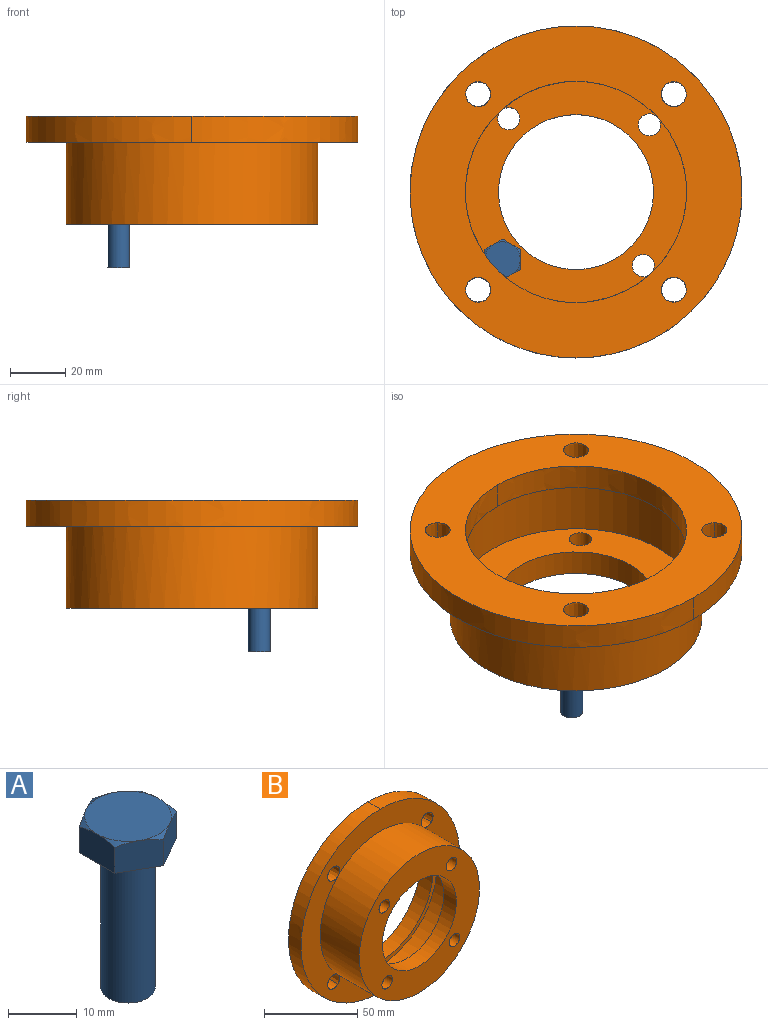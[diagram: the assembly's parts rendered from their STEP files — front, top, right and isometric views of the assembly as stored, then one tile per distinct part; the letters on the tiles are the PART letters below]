
ASSEMBLY  parts=2 mates=1
PART A: 16 faces, bbox 15.3x15.3x31.2 mm
  f0: cylinder r=3.97mm len=25.4mm, axis (0,0,-1), area 633.4mm2, adj f1,f2
  f1: plane 7.94x7.94mm, normal (0,0,-1), area 49.5mm2, adj f0
  f2: plane 14.66x12.7mm, normal (0,0,-1), area 90.2mm2, adj f0,f3,f4,f5,f6,f7,f8
  f3: plane 6.95x5.77mm, normal (-0.5,0.87,0), area 36.4mm2, adj f2,f4,f8,f12,f13
  f4: plane 7.94x5.77mm, normal (-1,0,0), area 36.4mm2, adj f2,f3,f5,f11,f12
  f5: plane 6.95x5.77mm, normal (-0.5,-0.87,0), area 36.4mm2, adj f2,f4,f6,f10,f11
  f6: plane 6.95x5.77mm, normal (0.5,-0.87,0), area 36.4mm2, adj f2,f5,f7,f9,f10
  f7: plane 7.94x5.77mm, normal (1,0,0), area 36.4mm2, adj f2,f6,f8,f9,f14
  f8: plane 6.95x5.77mm, normal (0.5,0.87,0), area 36.4mm2, adj f2,f3,f7,f13,f14
  f9: cone r=6.35mm half-angle=60deg, axis (0,0,-1), area 4mm2, adj f6,f7,f15
  f10: cone r=6.35mm half-angle=60deg, axis (0,0,-1), area 4mm2, adj f5,f6,f15
  f11: cone r=6.35mm half-angle=60deg, axis (0,0,-1), area 4mm2, adj f4,f5,f15
  f12: cone r=6.35mm half-angle=60deg, axis (0,0,-1), area 4mm2, adj f3,f4,f15
  f13: cone r=6.35mm half-angle=60deg, axis (0,0,-1), area 4mm2, adj f3,f8,f15
  f14: cone r=6.35mm half-angle=60deg, axis (0,0,-1), area 4mm2, adj f7,f8,f15
  f15: plane 12.7x12.7mm, normal (0,0,1), area 126.7mm2, adj f9,f10,f11,f12,f13,f14
PART B: 24 faces, bbox 120x39.1x120 mm
  f0: plane 85.01x85.01mm, normal (0,-1,0), area 647.8mm2, adj f10,f12,f15
  f1: extruded ~9.53x7.68mm, area 134.6mm2, adj f6,f11,f14
  f2: extruded ~9.53x7.68mm, area 134.6mm2, adj f7,f11,f14
  f3: extruded ~9.53x7.68mm, area 134.6mm2, adj f8,f11,f14
  f4: extruded ~9.53x7.68mm, area 134.6mm2, adj f9,f11,f14
  f5: extruded ~120x60mm, area 1795.4mm2, adj f11,f13,f14
  f6: extruded ~9.53x7.68mm, area 134.6mm2, adj f1,f11,f14
  f7: extruded ~9.53x7.68mm, area 134.6mm2, adj f2,f11,f14
  f8: extruded ~9.53x7.68mm, area 134.6mm2, adj f3,f11,f14
  f9: extruded ~9.53x7.68mm, area 134.6mm2, adj f4,f11,f14
  f10: extruded ~80x40mm, area 1196.9mm2, adj f0,f12,f14
  f11: plane 120.02x120.02mm, normal (0,-1,0), area 4551.7mm2, adj f1,f2,f3,f4,f5,f6,f7,f8
  f12: extruded ~80x40mm, area 1196.9mm2, adj f0,f10,f14
  f13: extruded ~120x60mm, area 1795.4mm2, adj f5,f11,f14
  f14: plane 120.02x120.02mm, normal (0,1,0), area 6028.9mm2, adj f1,f2,f3,f4,f5,f6,f7,f8
  f15: cylinder r=42.5mm len=85mm, axis (0,1,0), area 5340.7mm2, adj f0,f17
  f16: cylinder r=45.5mm len=91mm, axis (0,1,0), area 8440.8mm2, adj f11,f18
  f17: plane 85x85mm, normal (0,1,0), area 3010.4mm2, adj f15,f19,f20,f21,f22,f23
  f18: plane 91x91mm, normal (0,-1,0), area 3839.8mm2, adj f16,f19,f20,f21,f22,f23
  f19: cylinder r=4mm len=9.53mm, axis (0,-1,0), area 239.4mm2, adj f17,f18
  f20: cylinder r=4mm len=9.53mm, axis (0,-1,0), area 239.4mm2, adj f17,f18
  f21: cylinder r=28mm len=56mm, axis (0,-1,0), area 1675.7mm2, adj f17,f18
  f22: cylinder r=4mm len=9.53mm, axis (0,-1,0), area 239.4mm2, adj f17,f18
  f23: cylinder r=4mm len=9.53mm, axis (0,-1,0), area 239.4mm2, adj f17,f18
PLACE A t=(-124.79,30.6,26.55)mm
PLACE B rot(axis=(1,0,0),90deg) t=(-98.24,54.92,160.47)mm
MATE fastened B.f19 <-> A.f0  axis (0,0,-1) through (-124.79,30.6,51.95)mm
